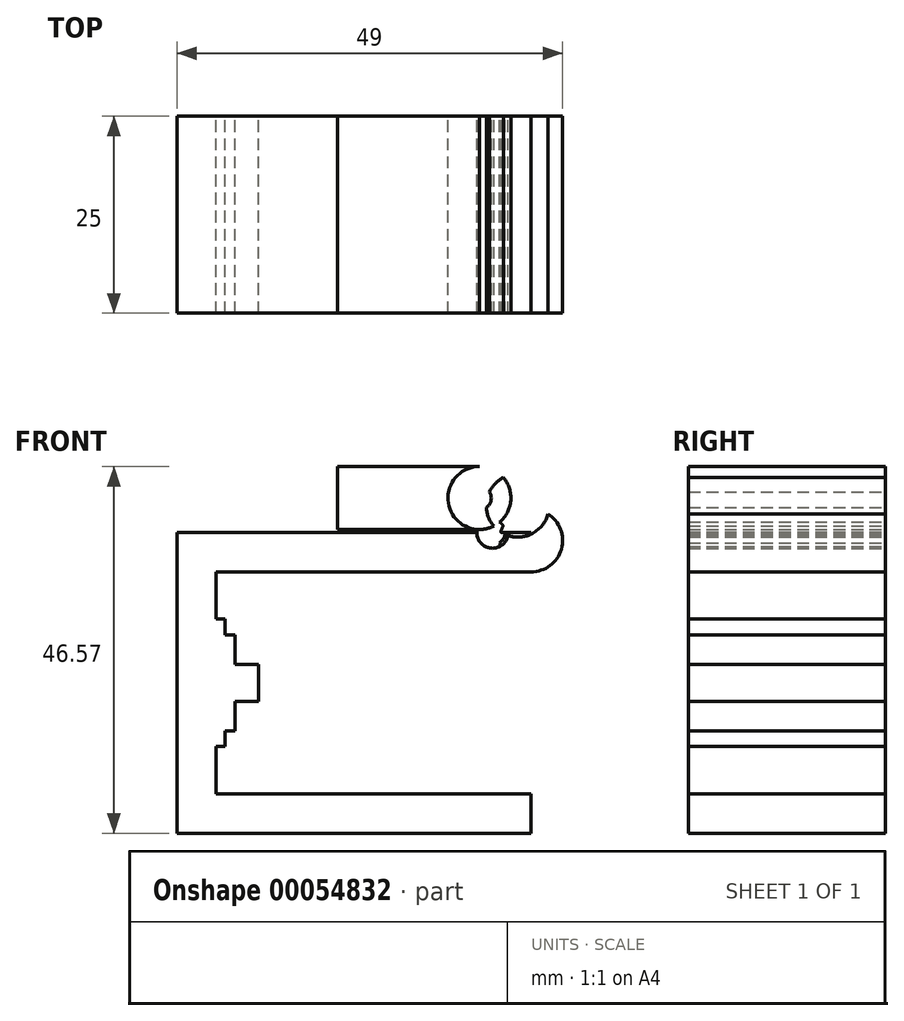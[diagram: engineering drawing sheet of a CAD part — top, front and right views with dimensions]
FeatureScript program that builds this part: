
annotation { "Feature Type Name" : "Feature", "Feature Type Description" : "" }
export const myFeature = defineFeature(function(context is Context, id is Id, definition is map)
    precondition{}
    {
        {
            var Q0;
            Q0=qCreatedBy(makeId("Front.planeOp"),FACE);
            var sketch = newSketch(context, id + "F0", { "sketchPlane" : qUnion([Q0])});
            skLineSegment(sketch, "E0", {"start": v(40, 19.1) * mm, "end": v(40, 14.1) * mm});
            skLineSegment(sketch, "E1", {"start": v(40, 14.1) * mm, "end": v(0, 14.1) * mm});
            skLineSegment(sketch, "E2", {"start": v(0, 14.1) * mm, "end": v(0, 8.1) * mm});
            skLineSegment(sketch, "E3", {"start": v(0, 8.1) * mm, "end": v(1.15, 8.1) * mm});
            skLineSegment(sketch, "E4", {"start": v(1.15, 8.1) * mm, "end": v(1.15, 6.1) * mm});
            skLineSegment(sketch, "E5", {"start": v(1.15, 6.1) * mm, "end": v(2.4, 6.1) * mm});
            skLineSegment(sketch, "E6", {"start": v(2.4, 6.1) * mm, "end": v(2.4, 2.35) * mm});
            skLineSegment(sketch, "E7", {"start": v(2.4, 2.35) * mm, "end": v(5.4, 2.35) * mm});
            skLineSegment(sketch, "E8", {"start": v(5.4, 2.35) * mm, "end": v(5.4, -2.35) * mm});
            skLineSegment(sketch, "E9", {"start": v(5.4, -2.35) * mm, "end": v(2.4, -2.35) * mm});
            skLineSegment(sketch, "E10", {"start": v(2.4, -2.35) * mm, "end": v(2.4, -6.1) * mm});
            skLineSegment(sketch, "E11", {"start": v(2.4, -6.1) * mm, "end": v(1.15, -6.1) * mm});
            skLineSegment(sketch, "E12", {"start": v(1.15, -6.1) * mm, "end": v(1.15, -8.1) * mm});
            skLineSegment(sketch, "E13", {"start": v(1.15, -8.1) * mm, "end": v(0, -8.1) * mm});
            skLineSegment(sketch, "E14", {"start": v(0, -8.1) * mm, "end": v(0, -14.1) * mm});
            skLineSegment(sketch, "E15", {"start": v(0, 14.1) * mm, "end": v(0, -14.1) * mm, "construction": true});
            skLineSegment(sketch, "E16", {"start": v(58.91, 0) * mm, "end": v(-58.91, 0) * mm, "construction": true});
            skLineSegment(sketch, "E17", {"start": v(40, 19.1) * mm, "end": v(-5, 19.1) * mm});
            skLineSegment(sketch, "E18.MirrorCS", {"start": v(40, -14.1) * mm, "end": v(0, -14.1) * mm});
            skLineSegment(sketch, "E19.MirrorCS", {"start": v(40, -19.1) * mm, "end": v(40, -14.1) * mm});
            skLineSegment(sketch, "E20.MirrorCS", {"start": v(40, -19.1) * mm, "end": v(-5, -19.1) * mm});
            skLineSegment(sketch, "E21", {"start": v(-5, 19.1) * mm, "end": v(-5, -19.1) * mm});
            skCircle(sketch, "E22", {"center": v(40, 18.1) * mm, "radius": 4 * mm});
            skCircle(sketch, "E23", {"center": v(35.1, 19.1) * mm, "radius": 2 * mm});
            skCircle(sketch, "E24", {"center": v(35.1, 19.1) * mm, "radius": 1.6 * mm});
            skCircle(sketch, "E25", {"center": v(33.44, 23.47) * mm, "radius": 4 * mm});
            skLineSegment(sketch, "E26", {"start": v(37.1, 20.86) * mm, "end": v(37.1, 19.1) * mm});
            skCircle(sketch, "E27", {"center": v(33.44, 23.47) * mm, "radius": 1.5 * mm});
            skLineSegment(sketch, "E28", {"start": v(33.44, 27.47) * mm, "end": v(15.44, 27.47) * mm});
            skLineSegment(sketch, "E29", {"start": v(15.44, 27.47) * mm, "end": v(15.44, 19.47) * mm});
            skLineSegment(sketch, "E30", {"start": v(15.44, 19.47) * mm, "end": v(33.44, 19.47) * mm});
            skCircle(sketch, "E31", {"center": v(35.1, 19.1) * mm, "radius": 4.68 * mm, "construction": true});
            skCircle(sketch, "E32", {"center": v(38.3, 22.51) * mm, "radius": 4 * mm});
            skSolve(sketch);
        }
        {
            var Q0;
            {var subQ0=sQuery(id+"F0.wireOp",EDGE,"E22");var subQ5=sQuery(id+"F0.wireOp",EDGE,"E23");var subQ6=makeQuery(id+"F0.imprint","INTERSECT",VERTEX,{"disambiguationData":[OD(1.0)],"derivedFrom":[subQ0,subQ5]});Q0=makeQuery(id+"F0.imprint","IMPRINT",FACE,{"disambiguationData":[TD([[makeQuery(id+"F0.imprint","IMPRINT",EDGE,{"disambiguationData":[TD([[subQ6,-1.0]])],"derivedFrom":subQ5}),-1.0]])]});}
            var Q1;
            {var subQ0=sQuery(id+"F0.wireOp",EDGE,"E22");var subQ3=sQuery(id+"F0.wireOp",EDGE,"E32");var subQ5=makeQuery(id+"F0.imprint","INTERSECT",VERTEX,{"disambiguationData":[OD(0.0)],"derivedFrom":[subQ0,subQ3]});Q1=makeQuery(id+"F0.imprint","IMPRINT",FACE,{"disambiguationData":[TD([[makeQuery(id+"F0.imprint","IMPRINT",EDGE,{"disambiguationData":[TD([[subQ5,1.0]])],"derivedFrom":subQ3}),-1.0]])]});}
            var Q2;
            {var subQ1=sQuery(id+"F0.wireOp",EDGE,"E1");Q2=makeQuery(id+"F0.imprint","IMPRINT",FACE,{"disambiguationData":[TD([[makeQuery(id+"F0.imprint","IMPRINT",EDGE,{"derivedFrom":subQ1}),-1.0]])]});}
            extrude(context, id + "F1", {"entities" : qUnion([Q0, Q1, Q2]), "depth" : 25 * mm});
        }
        {
            var Q0;
            {var subQ1=sQuery(id+"F0.wireOp",EDGE,"E28");Q0=makeQuery(id+"F0.imprint","IMPRINT",FACE,{"disambiguationData":[TD([[makeQuery(id+"F0.imprint","IMPRINT",EDGE,{"derivedFrom":subQ1}),1.0]])]});}
            var Q1;
            {var subQ0=sQuery(id+"F0.wireOp",EDGE,"E32");var subQ6=sQuery(id+"F0.wireOp",EDGE,"E23");var subQ9=makeQuery(id+"F0.imprint","INTERSECT",VERTEX,{"disambiguationData":[OD(0.0)],"derivedFrom":[subQ6,subQ0]});Q1=makeQuery(id+"F0.imprint","IMPRINT",FACE,{"disambiguationData":[TD([[makeQuery(id+"F0.imprint","IMPRINT",EDGE,{"disambiguationData":[TD([[subQ9,-1.0]])],"derivedFrom":subQ6}),-1.0]])]});}
            var Q2;
            {var subQ4=sQuery(id+"F0.wireOp",EDGE,"E23");var subQ6=sQuery(id+"F0.wireOp",EDGE,"E25");var subQ8=makeQuery(id+"F0.imprint","INTERSECT",VERTEX,{"disambiguationData":[OD(0.0)],"derivedFrom":[subQ4,subQ6]});Q2=makeQuery(id+"F0.imprint","IMPRINT",FACE,{"disambiguationData":[TD([[makeQuery(id+"F0.imprint","IMPRINT",EDGE,{"disambiguationData":[TD([[subQ8,-1.0]])],"derivedFrom":subQ4}),-1.0]])]});}
            var Q3;
            {var subQ0=sQuery(id+"F0.wireOp",EDGE,"E22");var subQ1=sQuery(id+"F0.wireOp",EDGE,"E17");var subQ2=makeQuery(id+"F0.imprint","INTERSECT",VERTEX,{"derivedFrom":[subQ1,subQ0]});Q3=makeQuery(id+"F0.imprint","IMPRINT",FACE,{"disambiguationData":[TD([[makeQuery(id+"F0.imprint","IMPRINT",EDGE,{"disambiguationData":[TD([[subQ2,-1.0]])],"derivedFrom":subQ1}),1.0]])]});}
            var Q4;
            {var subQ5=sQuery(id+"F0.wireOp",EDGE,"E22");var subQ6=sQuery(id+"F0.wireOp",EDGE,"E17");var subQ7=makeQuery(id+"F0.imprint","INTERSECT",VERTEX,{"derivedFrom":[subQ6,subQ5]});Q4=makeQuery(id+"F0.imprint","IMPRINT",FACE,{"disambiguationData":[TD([[makeQuery(id+"F0.imprint","IMPRINT",EDGE,{"disambiguationData":[TD([[subQ7,-1.0]])],"derivedFrom":subQ6}),-1.0]])]});}
            var Q5;
            {var subQ0=sQuery(id+"F0.wireOp",EDGE,"E25");var subQ1=sQuery(id+"F0.wireOp",EDGE,"E24");var subQ2=makeQuery(id+"F0.imprint","INTERSECT",VERTEX,{"disambiguationData":[OD(0.0)],"derivedFrom":[subQ1,subQ0]});Q5=makeQuery(id+"F0.imprint","IMPRINT",FACE,{"disambiguationData":[TD([[makeQuery(id+"F0.imprint","IMPRINT",EDGE,{"disambiguationData":[TD([[subQ2,-1.0]])],"derivedFrom":subQ1}),1.0]])]});}
            var Q6;
            {var subQ0=sQuery(id+"F0.wireOp",EDGE,"E24");var subQ1=sQuery(id+"F0.wireOp",EDGE,"E22");var subQ2=makeQuery(id+"F0.imprint","INTERSECT",VERTEX,{"disambiguationData":[OD(0.0)],"derivedFrom":[subQ1,subQ0]});Q6=makeQuery(id+"F0.imprint","IMPRINT",FACE,{"disambiguationData":[TD([[makeQuery(id+"F0.imprint","IMPRINT",EDGE,{"disambiguationData":[TD([[subQ2,-1.0]])],"derivedFrom":subQ1}),-1.0]])]});}
            var Q7;
            {var subQ0=sQuery(id+"F0.wireOp",EDGE,"E25");var subQ1=sQuery(id+"F0.wireOp",EDGE,"E23");var subQ2=makeQuery(id+"F0.imprint","INTERSECT",VERTEX,{"disambiguationData":[OD(0.0)],"derivedFrom":[subQ1,subQ0]});Q7=makeQuery(id+"F0.imprint","IMPRINT",FACE,{"disambiguationData":[TD([[makeQuery(id+"F0.imprint","IMPRINT",EDGE,{"disambiguationData":[TD([[subQ2,-1.0]])],"derivedFrom":subQ1}),1.0]])]});}
            var Q8;
            {var subQ0=sQuery(id+"F0.wireOp",EDGE,"E32");var subQ1=sQuery(id+"F0.wireOp",EDGE,"E24");var subQ2=makeQuery(id+"F0.imprint","INTERSECT",VERTEX,{"disambiguationData":[OD(0.0)],"derivedFrom":[subQ1,subQ0]});Q8=makeQuery(id+"F0.imprint","IMPRINT",FACE,{"disambiguationData":[TD([[makeQuery(id+"F0.imprint","IMPRINT",EDGE,{"disambiguationData":[TD([[subQ2,-1.0]])],"derivedFrom":subQ1}),1.0]])]});}
            var Q9;
            {var subQ0=sQuery(id+"F0.wireOp",EDGE,"E32");var subQ1=sQuery(id+"F0.wireOp",EDGE,"E17");var subQ2=makeQuery(id+"F0.imprint","INTERSECT",VERTEX,{"derivedFrom":[subQ1,subQ0]});Q9=makeQuery(id+"F0.imprint","IMPRINT",FACE,{"disambiguationData":[TD([[makeQuery(id+"F0.imprint","IMPRINT",EDGE,{"disambiguationData":[TD([[subQ2,-1.0]])],"derivedFrom":subQ1}),1.0]])]});}
            var Q10;
            {var subQ4=sQuery(id+"F0.wireOp",EDGE,"E32");var subQ5=sQuery(id+"F0.wireOp",EDGE,"E23");var subQ6=makeQuery(id+"F0.imprint","INTERSECT",VERTEX,{"disambiguationData":[OD(0.0)],"derivedFrom":[subQ5,subQ4]});Q10=makeQuery(id+"F0.imprint","IMPRINT",FACE,{"disambiguationData":[TD([[makeQuery(id+"F0.imprint","IMPRINT",EDGE,{"disambiguationData":[TD([[subQ6,-1.0]])],"derivedFrom":subQ5}),1.0]])]});}
            var Q11;
            {var subQ0=sQuery(id+"F0.wireOp",EDGE,"E24");var subQ1=sQuery(id+"F0.wireOp",EDGE,"E17");var subQ2=makeQuery(id+"F0.imprint","INTERSECT",VERTEX,{"disambiguationData":[OD(0.0)],"derivedFrom":[subQ1,subQ0]});Q11=makeQuery(id+"F0.imprint","IMPRINT",FACE,{"disambiguationData":[TD([[makeQuery(id+"F0.imprint","IMPRINT",EDGE,{"disambiguationData":[TD([[subQ2,-1.0]])],"derivedFrom":subQ1}),-1.0]])]});}
            var Q12;
            {var subQ0=sQuery(id+"F0.wireOp",EDGE,"E24");var subQ1=sQuery(id+"F0.wireOp",EDGE,"E17");var subQ2=makeQuery(id+"F0.imprint","INTERSECT",VERTEX,{"disambiguationData":[OD(0.0)],"derivedFrom":[subQ1,subQ0]});Q12=makeQuery(id+"F0.imprint","IMPRINT",FACE,{"disambiguationData":[TD([[makeQuery(id+"F0.imprint","IMPRINT",EDGE,{"disambiguationData":[TD([[subQ2,-1.0]])],"derivedFrom":subQ1}),1.0]])]});}
            var Q13;
            {var subQ0=sQuery(id+"F0.wireOp",EDGE,"E32");var subQ1=sQuery(id+"F0.wireOp",EDGE,"E17");var subQ2=makeQuery(id+"F0.imprint","INTERSECT",VERTEX,{"derivedFrom":[subQ1,subQ0]});Q13=makeQuery(id+"F0.imprint","IMPRINT",FACE,{"disambiguationData":[TD([[makeQuery(id+"F0.imprint","IMPRINT",EDGE,{"disambiguationData":[TD([[subQ2,-1.0]])],"derivedFrom":subQ1}),-1.0]])]});}
            extrude(context, id + "F2", {"entities" : qUnion([Q0, Q1, Q2, Q3, Q4, Q5, Q6, Q7, Q8, Q9, Q10, Q11, Q12, Q13]), "depth" : 25 * mm});
        }
    });
